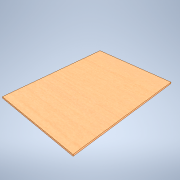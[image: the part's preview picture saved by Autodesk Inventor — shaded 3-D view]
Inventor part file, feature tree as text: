
AUTODESK INVENTOR PART (.ipt)
format: ipt  version: 2021 (Build 250183000, 183)  size: 104,448 bytes
history: native  units: mm
features: extrude x1, sketch x1
ambient origin geometry x8: Origin, YZ Plane, XZ Plane, XY Plane, X Axis, Y Axis, Z Axis, Center Point
bodies: Solid1 (feature_tree)
feature tree (2):
  extrude  "Extrusion1"  Depth=194.0mm
  sketch  "Sketch1"  dims[d0=143.5mm d1=194.0mm d2=3.0mm d3=0.0mm]
